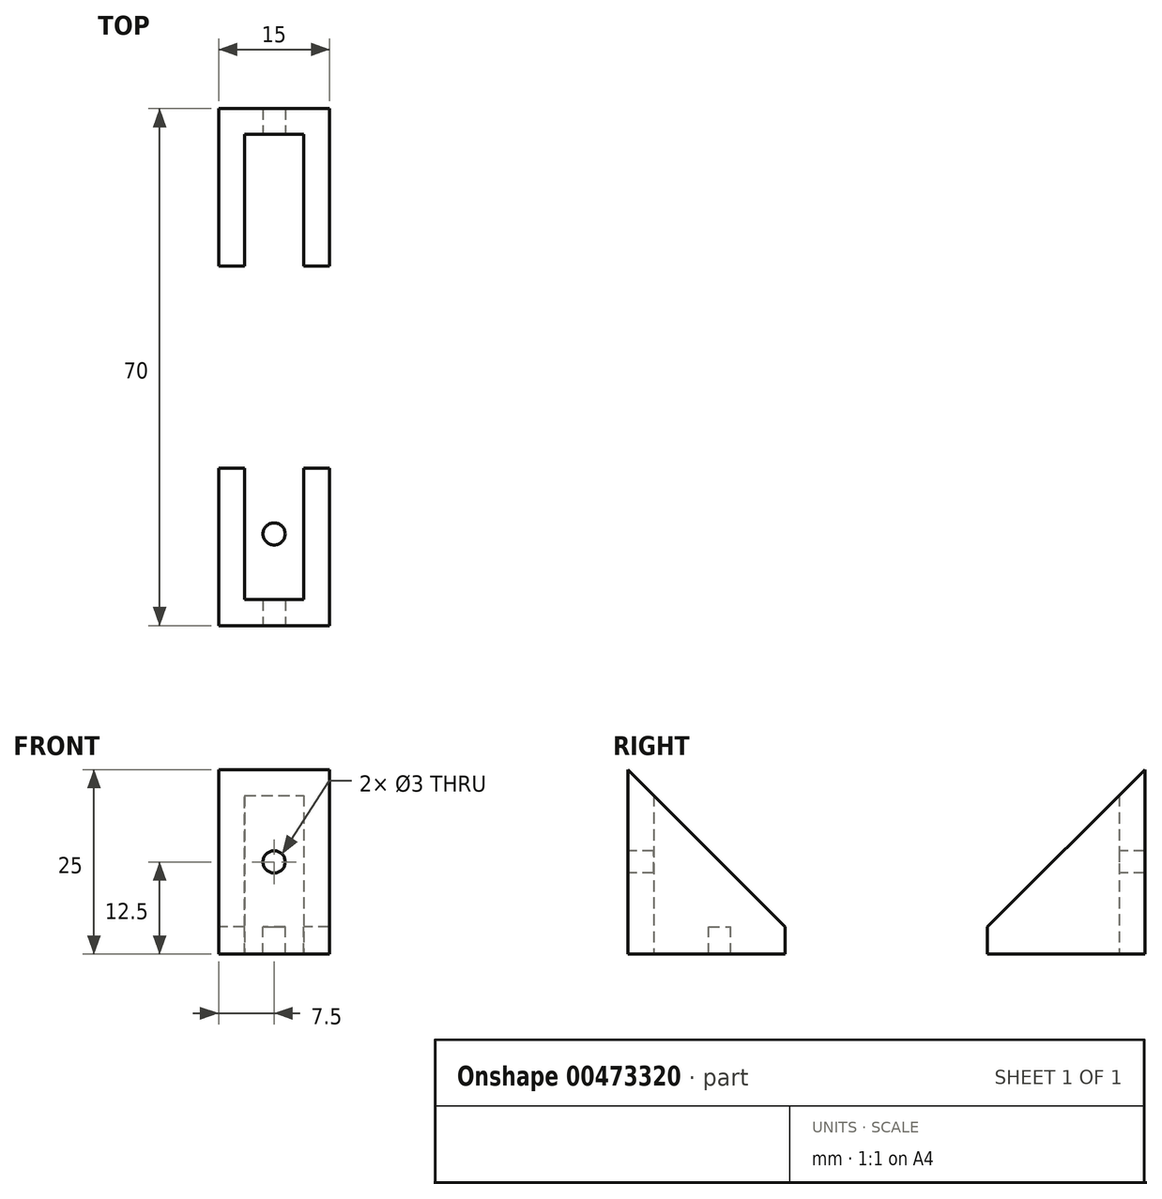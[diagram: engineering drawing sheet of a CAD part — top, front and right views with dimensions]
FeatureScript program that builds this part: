
annotation { "Feature Type Name" : "Feature", "Feature Type Description" : "" }
export const myFeature = defineFeature(function(context is Context, id is Id, definition is map)
    precondition{}
    {
        {
            var Q0;
            Q0=qCreatedBy(makeId("Top.planeOp"),FACE);
            var sketch = newSketch(context, id + "F0", { "sketchPlane" : qUnion([Q0])});
            skLineSegment(sketch, "E0.bottom", {"start": v(0, 0) * mm, "end": v(15, 0) * mm});
            skLineSegment(sketch, "E0.top", {"start": v(0, 70) * mm, "end": v(15, 70) * mm});
            skLineSegment(sketch, "E0.left", {"start": v(0, 0) * mm, "end": v(0, 70) * mm});
            skLineSegment(sketch, "E0.right", {"start": v(15, 0) * mm, "end": v(15, 70) * mm});
            skSolve(sketch);
        }
        {
            var Q0;
            Q0 = qSketchRegion(id + "F0", true);
            extrude(context, id + "F1", {"entities" : qUnion([Q0]), "depth" : 25 * mm});
        }
        {
            var Q0;
            Q0=makeQuery(id+"F1.opExtrude","SWEPT_FACE",FACE,{"disambiguationData":[OSD([sQuery(id+"F0.wireOp",EDGE,"E0.left")])]});
            var sketch = newSketch(context, id + "F2", { "sketchPlane" : qUnion([Q0])});
            skLineSegment(sketch, "E1", {"start": v(-35, 25) * mm, "end": v(-35, 0) * mm, "construction": true});
            skLineSegment(sketch, "E2", {"start": v(-70, 25) * mm, "end": v(-48.68, 3.68) * mm});
            skLineSegment(sketch, "E3", {"start": v(-48.68, 3.68) * mm, "end": v(-35, 3.68) * mm});
            skLineSegment(sketch, "E4", {"start": v(-70, 25) * mm, "end": v(-35, 25) * mm});
            skLineSegment(sketch, "E5.MirrorCS", {"start": v(0, 25) * mm, "end": v(-35, 25) * mm});
            skLineSegment(sketch, "E6.MirrorCS", {"start": v(-21.32, 3.68) * mm, "end": v(-35, 3.68) * mm});
            skLineSegment(sketch, "E7.MirrorCS", {"start": v(0, 25) * mm, "end": v(-21.32, 3.68) * mm});
            skSolve(sketch);
        }
        {
            var Q0;
            Q0=makeQuery(id+"F2.imprint","IMPRINT",FACE,{"disambiguationData":[TD([[makeQuery(id+"F2.imprint","IMPRINT",EDGE,{"derivedFrom":sQuery(id+"F2.wireOp",EDGE,"E2")}),1.0]])]});
            extrude(context, id + "F3", {"entities" : qUnion([Q0]), "operationType" : NewBodyOperationType.REMOVE, "oppositeDirection" : true, "depth" : 25 * mm});
        }
        {
            var Q0;
            Q0=makeQuery(id+"F3.boolean.opBoolean","COPY",FACE,{"derivedFrom":makeQuery(id+"F3.opExtrude","SWEPT_FACE",FACE,{"disambiguationData":[OSD([sQuery(id+"F2.wireOp",EDGE,"E3"),sQuery(id+"F2.wireOp",EDGE,"E6.MirrorCS")])]})});
            var sketch = newSketch(context, id + "F4", { "sketchPlane" : qUnion([Q0])});
            skLineSegment(sketch, "E8.0", {"start": v(0, 0) * mm, "end": v(15, 0) * mm});
            skLineSegment(sketch, "E9.top", {"start": v(5, 0) * mm, "end": v(10, 0) * mm});
            skLineSegment(sketch, "E10", {"start": v(0, 35) * mm, "end": v(15, 35) * mm, "construction": true});
            skLineSegment(sketch, "E11", {"start": v(3.5, 35) * mm, "end": v(3.5, 66.5) * mm});
            skLineSegment(sketch, "E12", {"start": v(3.5, 66.5) * mm, "end": v(11.5, 66.5) * mm});
            skLineSegment(sketch, "E13", {"start": v(11.5, 66.5) * mm, "end": v(11.5, 35) * mm});
            skLineSegment(sketch, "E14.MirrorCS", {"start": v(3.5, 35) * mm, "end": v(3.5, 3.5) * mm});
            skLineSegment(sketch, "E15.MirrorCS", {"start": v(11.5, 3.5) * mm, "end": v(11.5, 35) * mm});
            skLineSegment(sketch, "E16.MirrorCS", {"start": v(3.5, 3.5) * mm, "end": v(11.5, 3.5) * mm});
            skSolve(sketch);
        }
        {
            var Q0;
            Q0 = qSketchRegion(id + "F4", true);
            extrude(context, id + "F5", {"entities" : qUnion([Q0]), "operationType" : NewBodyOperationType.REMOVE, "depth" : 25 * mm});
        }
        {
            var Q0;
            Q0=makeQuery(id+"F1.opExtrude","SWEPT_FACE",FACE,{"disambiguationData":[OSD([sQuery(id+"F0.wireOp",EDGE,"E0.bottom")])]});
            var sketch = newSketch(context, id + "F6", { "sketchPlane" : qUnion([Q0])});
            skCircle(sketch, "E17", {"center": v(7.5, 12.5) * mm, "radius": 1.5 * mm});
            skPoint(sketch, "E17.centerSnap0", {"position": v(0, 12.5) * mm});
            skPoint(sketch, "E17.centerSnap1", {"position": v(7.5, 25) * mm});
            skSolve(sketch);
        }
        {
            var Q0;
            Q0 = qSketchRegion(id + "F6", true);
            extrude(context, id + "F7", {"entities" : qUnion([Q0]), "operationType" : NewBodyOperationType.REMOVE, "oppositeDirection" : true, "depth" : 83.8 * mm});
        }
        {
            var Q0;
            Q0=makeQuery(id+"F5.boolean.opBoolean","MERGE",FACE,{"derivedFrom":[makeQuery(id+"F3.boolean.opBoolean","COPY",FACE,{"derivedFrom":makeQuery(id+"F3.opExtrude","SWEPT_FACE",FACE,{"disambiguationData":[OSD([sQuery(id+"F2.wireOp",EDGE,"E3"),sQuery(id+"F2.wireOp",EDGE,"E6.MirrorCS")])]})}),makeQuery(id+"F5.opExtrude","CAP_FACE",FACE,{"disambiguationData":[OSD([sQuery(id+"F4.wireOp",EDGE,"E11"),sQuery(id+"F4.wireOp",EDGE,"E12"),sQuery(id+"F4.wireOp",EDGE,"E13"),sQuery(id+"F4.wireOp",EDGE,"E14.MirrorCS"),sQuery(id+"F4.wireOp",EDGE,"E15.MirrorCS"),sQuery(id+"F4.wireOp",EDGE,"E16.MirrorCS")])],"isStart":true})]});
            var sketch = newSketch(context, id + "F8", { "sketchPlane" : qUnion([Q0])});
            skCircle(sketch, "E18", {"center": v(7.5, 57.59) * mm, "radius": 1.5 * mm});
            skPoint(sketch, "E18.centerSnap0", {"position": v(7.5, 66.5) * mm});
            skPoint(sketch, "E18.centerSnap1", {"position": v(3.5, 57.59) * mm});
            skLineSegment(sketch, "E19", {"start": v(0, 35) * mm, "end": v(15, 35) * mm, "construction": true});
            skCircle(sketch, "E20.MirrorC", {"center": v(7.5, 12.41) * mm, "radius": 1.5 * mm});
            skCircle(sketch, "E21", {"center": v(7.5, 35) * mm, "radius": 1.5 * mm});
            skSolve(sketch);
        }
        {
            var Q0;
            Q0=makeQuery(id+"F8.imprint","IMPRINT",FACE,{"disambiguationData":[TD([[makeQuery(id+"F8.imprint","IMPRINT",EDGE,{"derivedFrom":sQuery(id+"F8.wireOp",EDGE,"E18")}),1.0]])]});
            var Q1;
            Q1=makeQuery(id+"F8.imprint","IMPRINT",FACE,{"disambiguationData":[TD([[makeQuery(id+"F8.imprint","IMPRINT",EDGE,{"derivedFrom":sQuery(id+"F8.wireOp",EDGE,"E20.MirrorC")}),-1.0]])]});
            var Q2;
            Q2=makeQuery(id+"F8.imprint","IMPRINT",FACE,{"disambiguationData":[TD([[makeQuery(id+"F8.imprint","IMPRINT",EDGE,{"derivedFrom":sQuery(id+"F8.wireOp",EDGE,"E21")}),1.0]])]});
            extrude(context, id + "F9", {"entities" : qUnion([Q0, Q1, Q2]), "operationType" : NewBodyOperationType.REMOVE, "oppositeDirection" : true, "depth" : 25 * mm});
        }
    });
